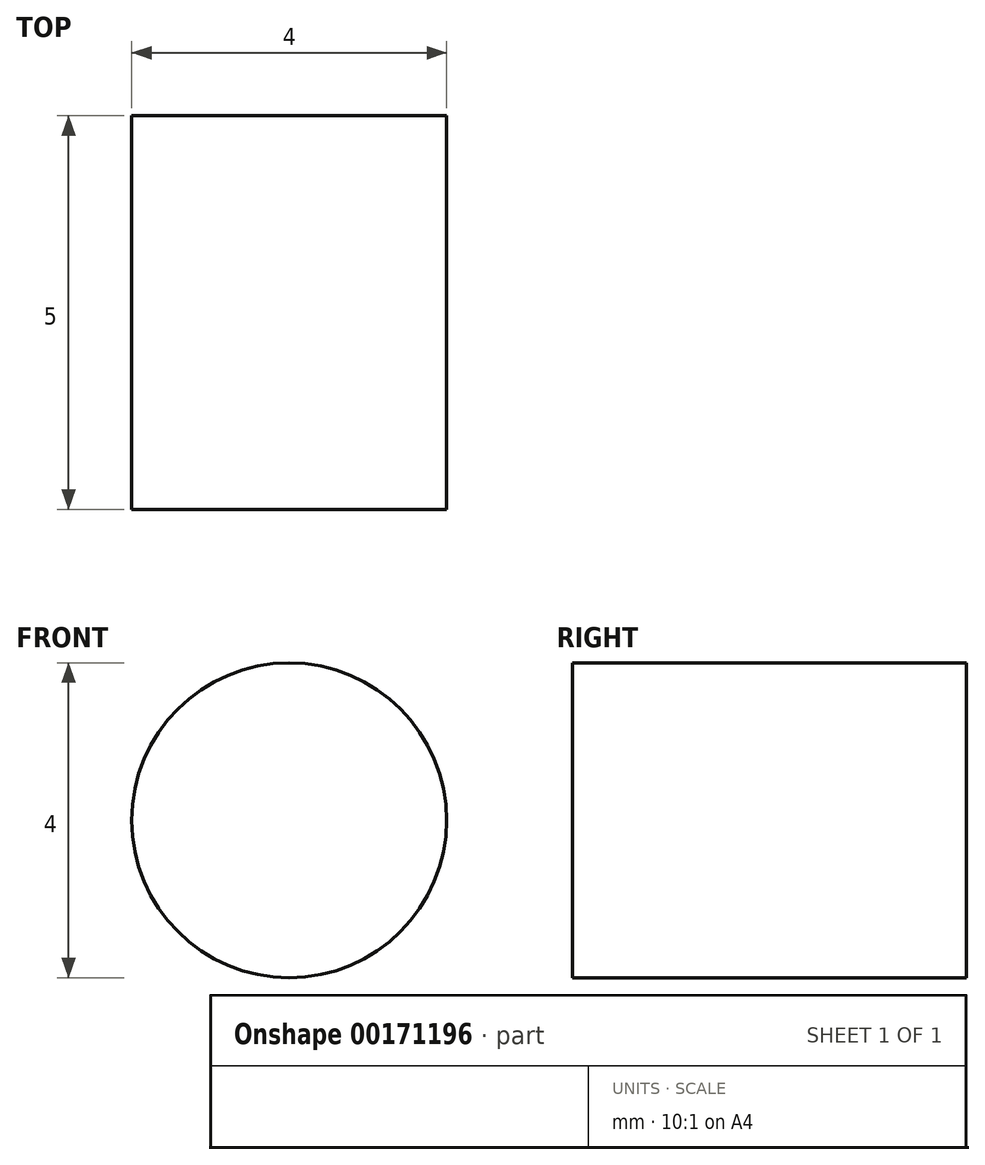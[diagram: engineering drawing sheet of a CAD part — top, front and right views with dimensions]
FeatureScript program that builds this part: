
annotation { "Feature Type Name" : "Feature", "Feature Type Description" : "" }
export const myFeature = defineFeature(function(context is Context, id is Id, definition is map)
    precondition{}
    {
        {
            var Q0;
            Q0=qCreatedBy(makeId("Front.planeOp"),FACE);
            var sketch = newSketch(context, id + "F0", { "sketchPlane" : qUnion([Q0])});
            skCircle(sketch, "E0", {"center": v(0, 0) * mm, "radius": 2 * mm});
            skLineSegment(sketch, "E1", {"start": v(1.98, 7.24) * mm, "end": v(0.92, 7.45) * mm});
            skArc(sketch, "E2", {"start": v(0.38, 9.17) * mm, "mid": v(0.3, 8.2) * mm, "end": v(0.92, 7.45) * mm});
            skArc(sketch, "E3", {"start": v(0.38, 9.17) * mm, "mid": v(0.36, 9.4) * mm, "end": v(0.3, 9.62) * mm});
            skLineSegment(sketch, "E4", {"start": v(0.3, 9.62) * mm, "end": v(0.21, 9.88) * mm});
            skArc(sketch, "E5", {"start": v(0.21, 9.88) * mm, "mid": v(-0.14, 10.6) * mm, "end": v(-0.6, 11.26) * mm});
            skLineSegment(sketch, "E6", {"start": v(-0.6, 11.26) * mm, "end": v(-0.77, 11.47) * mm});
            skLineSegment(sketch, "E7", {"start": v(-0.77, 11.47) * mm, "end": v(-0.87, 11.58) * mm});
            skLineSegment(sketch, "E8", {"start": v(-0.87, 11.58) * mm, "end": v(-1.89, 11.46) * mm});
            skLineSegment(sketch, "E9", {"start": v(-1.89, 11.46) * mm, "end": v(-1.96, 11.33) * mm});
            skLineSegment(sketch, "E10", {"start": v(-1.96, 11.33) * mm, "end": v(-2.08, 11.08) * mm});
            skArc(sketch, "E11", {"start": v(-2.08, 11.08) * mm, "mid": v(-2.37, 10.33) * mm, "end": v(-2.54, 9.55) * mm});
            skLineSegment(sketch, "E12", {"start": v(-2.54, 9.55) * mm, "end": v(-2.56, 9.28) * mm});
            skArc(sketch, "E13", {"start": v(-2.56, 9.28) * mm, "mid": v(-2.57, 9.05) * mm, "end": v(-2.53, 8.82) * mm});
            skArc(sketch, "E14", {"start": v(-2.65, 7.02) * mm, "mid": v(-2.22, 7.9) * mm, "end": v(-2.53, 8.82) * mm});
            skLineSegment(sketch, "E15", {"start": v(-2.65, 7.02) * mm, "end": v(-3.64, 6.57) * mm});
            skArc(sketch, "E16", {"start": v(-5.09, 7.64) * mm, "mid": v(-4.58, 6.8) * mm, "end": v(-3.64, 6.57) * mm});
            skArc(sketch, "E17", {"start": v(-5.09, 7.64) * mm, "mid": v(-5.23, 7.82) * mm, "end": v(-5.41, 7.96) * mm});
            skLineSegment(sketch, "E18", {"start": v(-5.41, 7.96) * mm, "end": v(-5.63, 8.12) * mm});
            skArc(sketch, "E19", {"start": v(-5.63, 8.12) * mm, "mid": v(-6.34, 8.5) * mm, "end": v(-7.1, 8.76) * mm});
            skLineSegment(sketch, "E20", {"start": v(-7.1, 8.76) * mm, "end": v(-7.37, 8.83) * mm});
            skLineSegment(sketch, "E21", {"start": v(-7.37, 8.83) * mm, "end": v(-7.51, 8.86) * mm});
            skLineSegment(sketch, "E22", {"start": v(-7.51, 8.86) * mm, "end": v(-8.27, 8.16) * mm});
            skLineSegment(sketch, "E23", {"start": v(-8.27, 8.16) * mm, "end": v(-8.25, 8.02) * mm});
            skLineSegment(sketch, "E24", {"start": v(-8.25, 8.02) * mm, "end": v(-8.2, 7.74) * mm});
            skArc(sketch, "E25", {"start": v(-8.2, 7.74) * mm, "mid": v(-7.99, 6.96) * mm, "end": v(-7.67, 6.23) * mm});
            skLineSegment(sketch, "E26", {"start": v(-7.67, 6.23) * mm, "end": v(-7.52, 6) * mm});
            skArc(sketch, "E27", {"start": v(-7.52, 6) * mm, "mid": v(-7.4, 5.81) * mm, "end": v(-7.23, 5.65) * mm});
            skArc(sketch, "E28", {"start": v(-6.27, 4.12) * mm, "mid": v(-6.44, 5.09) * mm, "end": v(-7.23, 5.65) * mm});
            skLineSegment(sketch, "E29", {"start": v(-6.27, 4.12) * mm, "end": v(-6.8, 3.18) * mm});
            skArc(sketch, "E30", {"start": v(-8.6, 3.2) * mm, "mid": v(-7.7, 2.81) * mm, "end": v(-6.8, 3.18) * mm});
            skArc(sketch, "E31", {"start": v(-8.6, 3.2) * mm, "mid": v(-8.83, 3.25) * mm, "end": v(-9.05, 3.26) * mm});
            skLineSegment(sketch, "E32", {"start": v(-9.05, 3.26) * mm, "end": v(-9.33, 3.26) * mm});
            skArc(sketch, "E33", {"start": v(-9.33, 3.26) * mm, "mid": v(-10.12, 3.15) * mm, "end": v(-10.89, 2.92) * mm});
            skLineSegment(sketch, "E34", {"start": v(-10.89, 2.92) * mm, "end": v(-11.15, 2.81) * mm});
            skLineSegment(sketch, "E35", {"start": v(-11.15, 2.81) * mm, "end": v(-11.29, 2.75) * mm});
            skLineSegment(sketch, "E36", {"start": v(-11.29, 2.75) * mm, "end": v(-11.48, 1.74) * mm});
            skLineSegment(sketch, "E37", {"start": v(-11.48, 1.74) * mm, "end": v(-11.38, 1.64) * mm});
            skLineSegment(sketch, "E38", {"start": v(-11.38, 1.64) * mm, "end": v(-11.18, 1.44) * mm});
            skArc(sketch, "E39", {"start": v(-11.18, 1.44) * mm, "mid": v(-10.56, 0.94) * mm, "end": v(-9.87, 0.53) * mm});
            skLineSegment(sketch, "E40", {"start": v(-9.87, 0.53) * mm, "end": v(-9.61, 0.43) * mm});
            skArc(sketch, "E41", {"start": v(-9.61, 0.43) * mm, "mid": v(-9.4, 0.35) * mm, "end": v(-9.17, 0.32) * mm});
            skArc(sketch, "E42", {"start": v(-7.5, -0.35) * mm, "mid": v(-8.2, 0.33) * mm, "end": v(-9.17, 0.32) * mm});
            skLineSegment(sketch, "E43", {"start": v(-7.5, -0.35) * mm, "end": v(-7.37, -1.43) * mm});
            skArc(sketch, "E44", {"start": v(-8.84, -2.48) * mm, "mid": v(-7.89, -2.26) * mm, "end": v(-7.37, -1.43) * mm});
            skArc(sketch, "E45", {"start": v(-8.84, -2.48) * mm, "mid": v(-9.05, -2.56) * mm, "end": v(-9.24, -2.69) * mm});
            skLineSegment(sketch, "E46", {"start": v(-9.24, -2.69) * mm, "end": v(-9.46, -2.85) * mm});
            skArc(sketch, "E47", {"start": v(-9.46, -2.85) * mm, "mid": v(-10.04, -3.4) * mm, "end": v(-10.52, -4.04) * mm});
            skLineSegment(sketch, "E48", {"start": v(-10.52, -4.04) * mm, "end": v(-10.67, -4.28) * mm});
            skLineSegment(sketch, "E49", {"start": v(-10.67, -4.28) * mm, "end": v(-10.75, -4.4) * mm});
            skLineSegment(sketch, "E50", {"start": v(-10.75, -4.4) * mm, "end": v(-10.32, -5.34) * mm});
            skLineSegment(sketch, "E51", {"start": v(-10.32, -5.34) * mm, "end": v(-10.17, -5.36) * mm});
            skLineSegment(sketch, "E52", {"start": v(-10.17, -5.36) * mm, "end": v(-9.9, -5.4) * mm});
            skArc(sketch, "E53", {"start": v(-9.9, -5.4) * mm, "mid": v(-9.1, -5.45) * mm, "end": v(-8.3, -5.37) * mm});
            skLineSegment(sketch, "E54", {"start": v(-8.3, -5.37) * mm, "end": v(-8.03, -5.3) * mm});
            skArc(sketch, "E55", {"start": v(-8.03, -5.3) * mm, "mid": v(-7.81, -5.24) * mm, "end": v(-7.61, -5.13) * mm});
            skArc(sketch, "E56", {"start": v(-5.86, -4.7) * mm, "mid": v(-6.83, -4.55) * mm, "end": v(-7.61, -5.13) * mm});
            skLineSegment(sketch, "E57", {"start": v(-5.86, -4.7) * mm, "end": v(-5.12, -5.49) * mm});
            skArc(sketch, "E58", {"start": v(-5.7, -7.2) * mm, "mid": v(-5.06, -6.46) * mm, "end": v(-5.12, -5.49) * mm});
            skArc(sketch, "E59", {"start": v(-5.7, -7.2) * mm, "mid": v(-5.82, -7.4) * mm, "end": v(-5.9, -7.6) * mm});
            skLineSegment(sketch, "E60", {"start": v(-5.9, -7.6) * mm, "end": v(-5.98, -7.87) * mm});
            skArc(sketch, "E61", {"start": v(-5.98, -7.87) * mm, "mid": v(-6.12, -8.65) * mm, "end": v(-6.14, -9.45) * mm});
            skLineSegment(sketch, "E62", {"start": v(-6.14, -9.45) * mm, "end": v(-6.12, -9.74) * mm});
            skLineSegment(sketch, "E63", {"start": v(-6.12, -9.74) * mm, "end": v(-6.1, -9.88) * mm});
            skLineSegment(sketch, "E64", {"start": v(-6.1, -9.88) * mm, "end": v(-5.2, -10.38) * mm});
            skLineSegment(sketch, "E65", {"start": v(-5.2, -10.38) * mm, "end": v(-5.08, -10.32) * mm});
            skLineSegment(sketch, "E66", {"start": v(-5.08, -10.32) * mm, "end": v(-4.83, -10.19) * mm});
            skArc(sketch, "E67", {"start": v(-4.83, -10.19) * mm, "mid": v(-4.15, -9.75) * mm, "end": v(-3.56, -9.22) * mm});
            skLineSegment(sketch, "E68", {"start": v(-3.56, -9.22) * mm, "end": v(-3.38, -9) * mm});
            skArc(sketch, "E69", {"start": v(-3.38, -9) * mm, "mid": v(-3.24, -8.83) * mm, "end": v(-3.14, -8.63) * mm});
            skArc(sketch, "E70", {"start": v(-1.98, -7.24) * mm, "mid": v(-2.85, -7.7) * mm, "end": v(-3.14, -8.63) * mm});
            skLineSegment(sketch, "E71", {"start": v(-1.98, -7.24) * mm, "end": v(-0.92, -7.45) * mm});
            skArc(sketch, "E72", {"start": v(-0.38, -9.17) * mm, "mid": v(-0.3, -8.2) * mm, "end": v(-0.92, -7.45) * mm});
            skArc(sketch, "E73", {"start": v(-0.38, -9.17) * mm, "mid": v(-0.36, -9.4) * mm, "end": v(-0.3, -9.62) * mm});
            skLineSegment(sketch, "E74", {"start": v(-0.3, -9.62) * mm, "end": v(-0.21, -9.88) * mm});
            skArc(sketch, "E75", {"start": v(-0.21, -9.88) * mm, "mid": v(0.14, -10.6) * mm, "end": v(0.6, -11.26) * mm});
            skLineSegment(sketch, "E76", {"start": v(0.6, -11.26) * mm, "end": v(0.77, -11.47) * mm});
            skLineSegment(sketch, "E77", {"start": v(0.77, -11.47) * mm, "end": v(0.87, -11.58) * mm});
            skLineSegment(sketch, "E78", {"start": v(0.87, -11.58) * mm, "end": v(1.89, -11.46) * mm});
            skLineSegment(sketch, "E79", {"start": v(1.89, -11.46) * mm, "end": v(1.96, -11.33) * mm});
            skLineSegment(sketch, "E80", {"start": v(1.96, -11.33) * mm, "end": v(2.08, -11.08) * mm});
            skArc(sketch, "E81", {"start": v(2.08, -11.08) * mm, "mid": v(2.37, -10.33) * mm, "end": v(2.54, -9.55) * mm});
            skLineSegment(sketch, "E82", {"start": v(2.54, -9.55) * mm, "end": v(2.56, -9.28) * mm});
            skArc(sketch, "E83", {"start": v(2.56, -9.28) * mm, "mid": v(2.57, -9.05) * mm, "end": v(2.53, -8.82) * mm});
            skArc(sketch, "E84", {"start": v(2.65, -7.02) * mm, "mid": v(2.22, -7.9) * mm, "end": v(2.53, -8.82) * mm});
            skLineSegment(sketch, "E85", {"start": v(2.65, -7.02) * mm, "end": v(3.64, -6.57) * mm});
            skArc(sketch, "E86", {"start": v(5.09, -7.64) * mm, "mid": v(4.58, -6.8) * mm, "end": v(3.64, -6.57) * mm});
            skArc(sketch, "E87", {"start": v(5.09, -7.64) * mm, "mid": v(5.23, -7.82) * mm, "end": v(5.41, -7.96) * mm});
            skLineSegment(sketch, "E88", {"start": v(5.41, -7.96) * mm, "end": v(5.63, -8.12) * mm});
            skArc(sketch, "E89", {"start": v(5.63, -8.12) * mm, "mid": v(6.34, -8.5) * mm, "end": v(7.1, -8.76) * mm});
            skLineSegment(sketch, "E90", {"start": v(7.1, -8.76) * mm, "end": v(7.37, -8.83) * mm});
            skLineSegment(sketch, "E91", {"start": v(7.37, -8.83) * mm, "end": v(7.51, -8.86) * mm});
            skLineSegment(sketch, "E92", {"start": v(7.51, -8.86) * mm, "end": v(8.27, -8.16) * mm});
            skLineSegment(sketch, "E93", {"start": v(8.27, -8.16) * mm, "end": v(8.25, -8.02) * mm});
            skLineSegment(sketch, "E94", {"start": v(8.25, -8.02) * mm, "end": v(8.2, -7.74) * mm});
            skArc(sketch, "E95", {"start": v(8.2, -7.74) * mm, "mid": v(7.99, -6.96) * mm, "end": v(7.67, -6.23) * mm});
            skLineSegment(sketch, "E96", {"start": v(7.67, -6.23) * mm, "end": v(7.52, -6) * mm});
            skArc(sketch, "E97", {"start": v(7.52, -6) * mm, "mid": v(7.4, -5.81) * mm, "end": v(7.23, -5.65) * mm});
            skArc(sketch, "E98", {"start": v(6.27, -4.12) * mm, "mid": v(6.44, -5.09) * mm, "end": v(7.23, -5.65) * mm});
            skLineSegment(sketch, "E99", {"start": v(6.27, -4.12) * mm, "end": v(6.8, -3.18) * mm});
            skArc(sketch, "E100", {"start": v(8.6, -3.2) * mm, "mid": v(7.7, -2.81) * mm, "end": v(6.8, -3.18) * mm});
            skArc(sketch, "E101", {"start": v(8.6, -3.2) * mm, "mid": v(8.83, -3.25) * mm, "end": v(9.05, -3.26) * mm});
            skLineSegment(sketch, "E102", {"start": v(9.05, -3.26) * mm, "end": v(9.33, -3.26) * mm});
            skArc(sketch, "E103", {"start": v(9.33, -3.26) * mm, "mid": v(10.12, -3.15) * mm, "end": v(10.89, -2.92) * mm});
            skLineSegment(sketch, "E104", {"start": v(10.89, -2.92) * mm, "end": v(11.15, -2.81) * mm});
            skLineSegment(sketch, "E105", {"start": v(11.15, -2.81) * mm, "end": v(11.29, -2.75) * mm});
            skLineSegment(sketch, "E106", {"start": v(11.29, -2.75) * mm, "end": v(11.48, -1.74) * mm});
            skLineSegment(sketch, "E107", {"start": v(11.48, -1.74) * mm, "end": v(11.38, -1.64) * mm});
            skLineSegment(sketch, "E108", {"start": v(11.38, -1.64) * mm, "end": v(11.18, -1.44) * mm});
            skArc(sketch, "E109", {"start": v(11.18, -1.44) * mm, "mid": v(10.56, -0.94) * mm, "end": v(9.87, -0.53) * mm});
            skLineSegment(sketch, "E110", {"start": v(9.87, -0.53) * mm, "end": v(9.61, -0.43) * mm});
            skArc(sketch, "E111", {"start": v(9.61, -0.43) * mm, "mid": v(9.4, -0.35) * mm, "end": v(9.17, -0.32) * mm});
            skArc(sketch, "E112", {"start": v(7.5, 0.35) * mm, "mid": v(8.2, -0.33) * mm, "end": v(9.17, -0.32) * mm});
            skLineSegment(sketch, "E113", {"start": v(7.5, 0.35) * mm, "end": v(7.37, 1.43) * mm});
            skArc(sketch, "E114", {"start": v(8.84, 2.48) * mm, "mid": v(7.89, 2.26) * mm, "end": v(7.37, 1.43) * mm});
            skArc(sketch, "E115", {"start": v(8.84, 2.48) * mm, "mid": v(9.05, 2.56) * mm, "end": v(9.24, 2.69) * mm});
            skLineSegment(sketch, "E116", {"start": v(9.24, 2.69) * mm, "end": v(9.46, 2.85) * mm});
            skArc(sketch, "E117", {"start": v(9.46, 2.85) * mm, "mid": v(10.04, 3.4) * mm, "end": v(10.52, 4.04) * mm});
            skLineSegment(sketch, "E118", {"start": v(10.52, 4.04) * mm, "end": v(10.67, 4.28) * mm});
            skLineSegment(sketch, "E119", {"start": v(10.67, 4.28) * mm, "end": v(10.75, 4.4) * mm});
            skLineSegment(sketch, "E120", {"start": v(10.75, 4.4) * mm, "end": v(10.32, 5.34) * mm});
            skLineSegment(sketch, "E121", {"start": v(10.32, 5.34) * mm, "end": v(10.17, 5.36) * mm});
            skLineSegment(sketch, "E122", {"start": v(10.17, 5.36) * mm, "end": v(9.9, 5.4) * mm});
            skArc(sketch, "E123", {"start": v(9.9, 5.4) * mm, "mid": v(9.1, 5.45) * mm, "end": v(8.3, 5.37) * mm});
            skLineSegment(sketch, "E124", {"start": v(8.3, 5.37) * mm, "end": v(8.03, 5.3) * mm});
            skArc(sketch, "E125", {"start": v(8.03, 5.3) * mm, "mid": v(7.81, 5.24) * mm, "end": v(7.61, 5.13) * mm});
            skArc(sketch, "E126", {"start": v(5.86, 4.7) * mm, "mid": v(6.83, 4.55) * mm, "end": v(7.61, 5.13) * mm});
            skLineSegment(sketch, "E127", {"start": v(5.86, 4.7) * mm, "end": v(5.12, 5.49) * mm});
            skArc(sketch, "E128", {"start": v(5.7, 7.2) * mm, "mid": v(5.06, 6.46) * mm, "end": v(5.12, 5.49) * mm});
            skArc(sketch, "E129", {"start": v(5.7, 7.2) * mm, "mid": v(5.82, 7.4) * mm, "end": v(5.9, 7.6) * mm});
            skLineSegment(sketch, "E130", {"start": v(5.9, 7.6) * mm, "end": v(5.98, 7.87) * mm});
            skArc(sketch, "E131", {"start": v(5.98, 7.87) * mm, "mid": v(6.12, 8.65) * mm, "end": v(6.14, 9.45) * mm});
            skLineSegment(sketch, "E132", {"start": v(6.14, 9.45) * mm, "end": v(6.12, 9.74) * mm});
            skLineSegment(sketch, "E133", {"start": v(6.12, 9.74) * mm, "end": v(6.1, 9.88) * mm});
            skLineSegment(sketch, "E134", {"start": v(6.1, 9.88) * mm, "end": v(5.2, 10.38) * mm});
            skLineSegment(sketch, "E135", {"start": v(5.2, 10.38) * mm, "end": v(5.08, 10.32) * mm});
            skLineSegment(sketch, "E136", {"start": v(5.08, 10.32) * mm, "end": v(4.83, 10.19) * mm});
            skArc(sketch, "E137", {"start": v(4.83, 10.19) * mm, "mid": v(4.15, 9.75) * mm, "end": v(3.56, 9.22) * mm});
            skLineSegment(sketch, "E138", {"start": v(3.56, 9.22) * mm, "end": v(3.38, 9) * mm});
            skArc(sketch, "E139", {"start": v(3.38, 9) * mm, "mid": v(3.24, 8.83) * mm, "end": v(3.14, 8.63) * mm});
            skArc(sketch, "E140", {"start": v(1.98, 7.24) * mm, "mid": v(2.85, 7.7) * mm, "end": v(3.14, 8.63) * mm});
            skSolve(sketch);
        }
        {
            var Q0;
            Q0=makeQuery(id+"F0.imprint","IMPRINT",FACE,{"disambiguationData":[TD([[makeQuery(id+"F0.imprint","IMPRINT",EDGE,{"derivedFrom":sQuery(id+"F0.wireOp",EDGE,"E0")}),1.0]])]});
            extrude(context, id + "F1", {"entities" : qUnion([Q0]), "depth" : 5 * mm});
        }
    });
